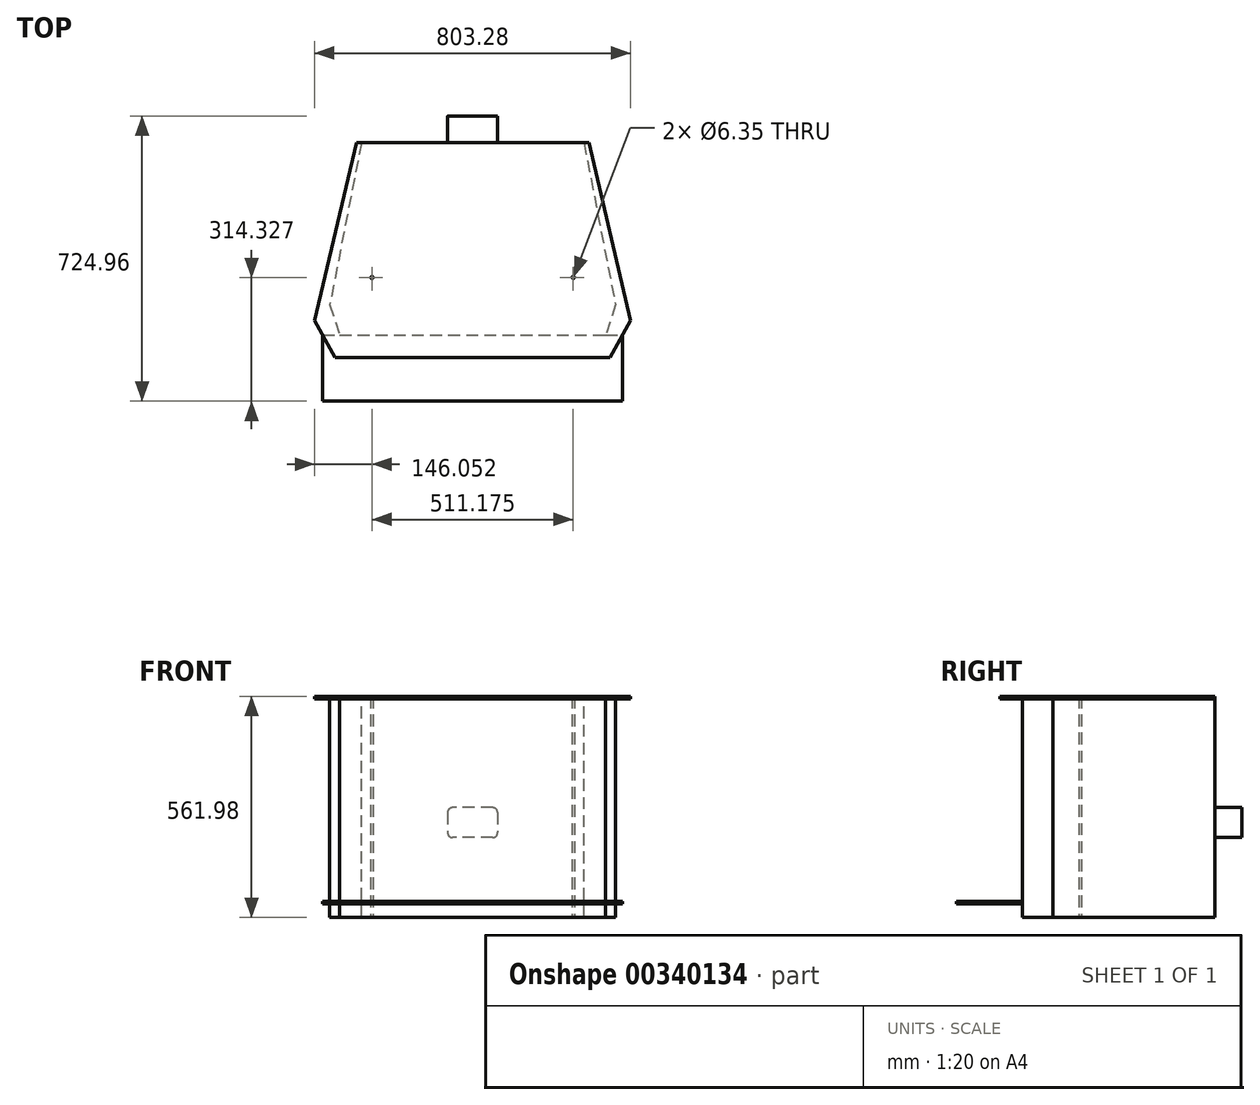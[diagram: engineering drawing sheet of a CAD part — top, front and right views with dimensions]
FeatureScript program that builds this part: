
annotation { "Feature Type Name" : "Feature", "Feature Type Description" : "" }
export const myFeature = defineFeature(function(context is Context, id is Id, definition is map)
    precondition{}
    {
        {
            var Q0;
            Q0=qCreatedBy(makeId("Top.planeOp"),FACE);
            var sketch = newSketch(context, id + "F0", { "sketchPlane" : qUnion([Q0])});
            skLineSegment(sketch, "E0", {"start": v(0, 278.02) * mm, "end": v(-295.27, 278.02) * mm});
            skLineSegment(sketch, "E1", {"start": v(-295.27, 278.02) * mm, "end": v(-401.64, -173.17) * mm});
            skLineSegment(sketch, "E2", {"start": v(-401.64, -173.17) * mm, "end": v(-349.25, -267.55) * mm});
            skLineSegment(sketch, "E3", {"start": v(-349.25, -267.55) * mm, "end": v(0, -267.55) * mm});
            skLineSegment(sketch, "E4.MirrorCS", {"start": v(0, 278.02) * mm, "end": v(295.27, 278.02) * mm});
            skLineSegment(sketch, "E5.MirrorCS", {"start": v(295.27, 278.02) * mm, "end": v(401.64, -173.17) * mm});
            skLineSegment(sketch, "E6.MirrorCS", {"start": v(401.64, -173.17) * mm, "end": v(349.25, -267.55) * mm});
            skLineSegment(sketch, "E7.MirrorCS", {"start": v(349.25, -267.55) * mm, "end": v(0, -267.55) * mm});
            skSolve(sketch);
        }
        {
            var Q0;
            Q0 = qSketchRegion(id + "F0", true);
            extrude(context, id + "F1", {"entities" : qUnion([Q0]), "depth" : 6.35 * mm});
        }
        {
            var Q0;
            Q0=makeQuery(id+"F1.opExtrude","CAP_FACE",FACE,{"disambiguationData":[OSD([sQuery(id+"F0.wireOp",EDGE,"E0"),sQuery(id+"F0.wireOp",EDGE,"E1"),sQuery(id+"F0.wireOp",EDGE,"E2"),sQuery(id+"F0.wireOp",EDGE,"E3"),sQuery(id+"F0.wireOp",EDGE,"E4.MirrorCS"),sQuery(id+"F0.wireOp",EDGE,"E5.MirrorCS"),sQuery(id+"F0.wireOp",EDGE,"E6.MirrorCS"),sQuery(id+"F0.wireOp",EDGE,"E7.MirrorCS")])],"isStart":true});
            var sketch = newSketch(context, id + "F2", { "sketchPlane" : qUnion([Q0])});
            skLineSegment(sketch, "E8", {"start": v(0, -278.02) * mm, "end": v(282.57, -278.02) * mm});
            skLineSegment(sketch, "E9", {"start": v(282.57, -278.02) * mm, "end": v(362.89, 133.32) * mm});
            skLineSegment(sketch, "E10", {"start": v(362.89, 133.32) * mm, "end": v(338.14, 210.4) * mm});
            skLineSegment(sketch, "E11", {"start": v(338.14, 210.4) * mm, "end": v(0, 210.4) * mm});
            skLineSegment(sketch, "E12.MirrorCS", {"start": v(0, -278.02) * mm, "end": v(-282.57, -278.02) * mm});
            skLineSegment(sketch, "E13.MirrorCS", {"start": v(-282.57, -278.02) * mm, "end": v(-362.89, 133.32) * mm});
            skLineSegment(sketch, "E14.MirrorCS", {"start": v(-362.89, 133.32) * mm, "end": v(-338.14, 210.4) * mm});
            skLineSegment(sketch, "E15.MirrorCS", {"start": v(-338.14, 210.4) * mm, "end": v(0, 210.4) * mm});
            skSolve(sketch);
        }
        {
            var Q0;
            Q0 = qSketchRegion(id + "F2", true);
            extrude(context, id + "F3", {"entities" : qUnion([Q0]), "operationType" : NewBodyOperationType.ADD, "flatOperationType" : FlatOperationType.REMOVE, "offsetDistance" : 25.4 * mm, "depth" : 555.62 * mm, "domain" : OperationDomain.MODEL});
        }
        {
            var Q0;
            Q0=makeQuery(id+"F3.boolean.opBoolean","MERGE",FACE,{"derivedFrom":[makeQuery(id+"F1.opExtrude","SWEPT_FACE",FACE,{"disambiguationData":[OSD([sQuery(id+"F0.wireOp",EDGE,"E0"),sQuery(id+"F0.wireOp",EDGE,"E4.MirrorCS")])]}),makeQuery(id+"F3.opExtrude","SWEPT_FACE",FACE,{"disambiguationData":[OSD([sQuery(id+"F2.wireOp",EDGE,"E8"),sQuery(id+"F2.wireOp",EDGE,"E12.MirrorCS")])]})]});
            var sketch = newSketch(context, id + "F4", { "sketchPlane" : qUnion([Q0])});
            skLineSegment(sketch, "E16.bottom", {"start": v(-63.5, -276.23) * mm, "end": v(63.5, -276.23) * mm});
            skLineSegment(sketch, "E16.top", {"start": v(-63.5, -352.43) * mm, "end": v(63.5, -352.43) * mm});
            skLineSegment(sketch, "E16.left", {"start": v(-63.5, -276.23) * mm, "end": v(-63.5, -352.43) * mm});
            skLineSegment(sketch, "E16.right", {"start": v(63.5, -276.23) * mm, "end": v(63.5, -352.43) * mm});
            skPoint(sketch, "E16.middle", {"position": v(0, -314.33) * mm});
            skSolve(sketch);
        }
        {
            var Q0;
            Q0 = qSketchRegion(id + "F4", true);
            extrude(context, id + "F5", {"entities" : qUnion([Q0]), "operationType" : NewBodyOperationType.ADD, "depth" : 68.26 * mm});
        }
        {
            var Q0;
            Q0=makeQuery(id+"F5.opExtrude","SWEPT_EDGE",EDGE,{"disambiguationData":[OSD([sQuery(id+"F4.wireOp",EDGE,"E16.bottom"),sQuery(id+"F4.wireOp",EDGE,"E16.left")])]});
            var Q1;
            Q1=makeQuery(id+"F5.opExtrude","SWEPT_EDGE",EDGE,{"disambiguationData":[OSD([sQuery(id+"F4.wireOp",EDGE,"E16.bottom"),sQuery(id+"F4.wireOp",EDGE,"E16.right")])]});
            var Q2;
            Q2=makeQuery(id+"F5.opExtrude","SWEPT_EDGE",EDGE,{"disambiguationData":[OSD([sQuery(id+"F4.wireOp",EDGE,"E16.top"),sQuery(id+"F4.wireOp",EDGE,"E16.right")])]});
            var Q3;
            Q3=makeQuery(id+"F5.opExtrude","SWEPT_EDGE",EDGE,{"disambiguationData":[OSD([sQuery(id+"F4.wireOp",EDGE,"E16.top"),sQuery(id+"F4.wireOp",EDGE,"E16.left")])]});
            fillet(context, id + "F6", {"entities" : qUnion([Q0, Q1, Q2, Q3]), "radius" : 12.7 * mm, "tangentPropagation" : true, "allowEdgeOverflow" : false});
        }
        {
            var Q0;
            Q0=makeQuery(id+"F1.opExtrude","CAP_FACE",FACE,{"disambiguationData":[OSD([sQuery(id+"F0.wireOp",EDGE,"E0"),sQuery(id+"F0.wireOp",EDGE,"E1"),sQuery(id+"F0.wireOp",EDGE,"E2"),sQuery(id+"F0.wireOp",EDGE,"E3"),sQuery(id+"F0.wireOp",EDGE,"E4.MirrorCS"),sQuery(id+"F0.wireOp",EDGE,"E5.MirrorCS"),sQuery(id+"F0.wireOp",EDGE,"E6.MirrorCS"),sQuery(id+"F0.wireOp",EDGE,"E7.MirrorCS")])],"isStart":false});
            var sketch = newSketch(context, id + "F7", { "sketchPlane" : qUnion([Q0])});
            skPoint(sketch, "E17", {"position": v(-255.59, -64.35) * mm});
            skPoint(sketch, "E18.MirrorP", {"position": v(255.59, -64.35) * mm});
            skLineSegment(sketch, "E19", {"start": v(-414.27, -64.35) * mm, "end": v(459.33, -64.35) * mm, "construction": true});
            skPoint(sketch, "E20", {"position": v(-375.99, -64.35) * mm});
            skPoint(sketch, "E21", {"position": v(375.99, -64.35) * mm});
            skSolve(sketch);
        }
        {
            var Q0;
            Q0=sQuery(id+"F7.wireOp",VERTEX,"E17");
            var Q1;
            Q1=sQuery(id+"F7.wireOp",VERTEX,"E18.MirrorP");
            var Q2;
            Q2=makeQuery(id+"F1.opExtrude","SWEPT_BODY",BODY,{"disambiguationData":[OSD([sQuery(id+"F0.wireOp",EDGE,"E0"),sQuery(id+"F0.wireOp",EDGE,"E1"),sQuery(id+"F0.wireOp",EDGE,"E2"),sQuery(id+"F0.wireOp",EDGE,"E3"),sQuery(id+"F0.wireOp",EDGE,"E4.MirrorCS"),sQuery(id+"F0.wireOp",EDGE,"E5.MirrorCS"),sQuery(id+"F0.wireOp",EDGE,"E6.MirrorCS"),sQuery(id+"F0.wireOp",EDGE,"E7.MirrorCS")])]});
            hole(context, id + "F8", {"style" : HoleStyle.SIMPLE, "endStyle" : HoleEndStyle.THROUGH, "holeDiameter" : 6.35 * mm, "tappedDepth" : 12.7 * mm, "tapClearance" : 3, "locations" : qUnion([Q0, Q1]), "scope" : qUnion([Q2]), "startStyle" : HoleStartStyle.PART});
        }
        {
            var Q0;
            Q0=makeQuery(id+"F3.opExtrude","SWEPT_FACE",FACE,{"disambiguationData":[OSD([sQuery(id+"F2.wireOp",EDGE,"E11"),sQuery(id+"F2.wireOp",EDGE,"E15.MirrorCS")])]});
            var sketch = newSketch(context, id + "F9", { "sketchPlane" : qUnion([Q0])});
            skLineSegment(sketch, "E22.bottom", {"start": v(-381, -514.35) * mm, "end": v(381, -514.35) * mm});
            skLineSegment(sketch, "E22.top", {"start": v(-381, -520.7) * mm, "end": v(381, -520.7) * mm});
            skLineSegment(sketch, "E22.left", {"start": v(-381, -514.35) * mm, "end": v(-381, -520.7) * mm});
            skLineSegment(sketch, "E22.right", {"start": v(381, -514.35) * mm, "end": v(381, -520.7) * mm});
            skPoint(sketch, "E22.middle", {"position": v(0, -517.52) * mm});
            skSolve(sketch);
        }
        {
            var Q0;
            Q0 = qSketchRegion(id + "F9", true);
            extrude(context, id + "F10", {"entities" : qUnion([Q0]), "operationType" : NewBodyOperationType.ADD, "depth" : 168.27 * mm});
        }
    });
